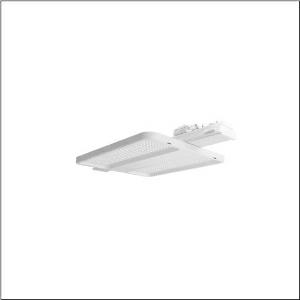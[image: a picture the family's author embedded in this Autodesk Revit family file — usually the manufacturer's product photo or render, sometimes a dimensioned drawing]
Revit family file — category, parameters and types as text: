
# Revit family: highbay_11_fur_licross_r__tragschiene_midi_51hn11da4fla_28e0
name_source: partatom
category: Lighting Fixtures
units: mm (PartAtom-declared; Revit-internal decimal feet)

## family parameters
Cut with Voids When Loaded = No
Host = Face
Light Source = No
Part Type = Normal
Room Calculation Point = No
Round Connector Dimension = Use Diameter
Shared = No

## types (1)
- --- (1 x LED, 15000 lm, 73.2 W, 4000K)
    Apparent Load = 73 VA
    CIE Flux Codes = 85 97 100 100 100
    Color Rendering = 80
    Color Temperature = 4000K
    Default Elevation = 1800 mm
    Description = Highbay 11 for Licross® trunking rail midi, high bay luminaire, primary light control with lens, of PMMA, primary optical cover: cover, of PMMA, light emission: direct distribution, primary light characteristic: symmetric, LED, rated luminous flux: 15.000lm, luminous efficacy: 205lm/W, light colour: 840, colour temperature: 4000K, control gear: DALI 2, with plug, 5-pole, with phase selection, mains connection: 230..240V, AC, 50/60Hz, rated input power: 73.2W, housing frame, of high-performance plastic PA6, matt traffic white (RAL 9016), length: 750mm, width: 442mm, height: 71mm, lever catch, fixing on rail side, of steel, galvanised, white, blank cover, of PC/ABS, traffic white (RAL 9016), protection rating (complete): IP64, insulation class (complete): insulation class I (protective earthing), certification: CE, ENEC, VDE, UKCA, protection symbol: D, impact resistance: IK07, permissible operating ambient temperature: -40..+55°C, corresponds to IFS (International Featured Standards) requirements for safety and quality in the food industry, LABS conformity tested according to VDMA 24364:2018-05, packaging unit: 1 piece
    Height = 72 mm  [stored 0.23622 ft]
    Lamp = 1 x LED
    Lamp Light Flux = 15000 lm
    Lamp Power = 73.2 W
    Lamp count = 1
    Length = 474 mm
    Luminous efficacy = 205 lm/W
    Manufacturer = Siteco
    ModVariant = No
    Model = 51HN11DA4FLA
    Mounting Place = Ceiling
    Mounting Type = Pendant
    Number of Poles = 1
    OnlyDefault = Yes
    Power Factor = 1
    Product Name = Highbay 11 für Licross® Tragschiene midi
    Product group = high bay luminaire
    ProductGroupID = 901
    Protection Class = Protection class I
    Protection Degree = IP 64
    RLX_Detail_Level = 1
    RLX_Emergency_Light_Flux = 0 lm
    RLX_Emergency_Type = 0
    RLX_Emergency_Type_DB = No
    RlxData = <blob elided: 16909 chars, md5=98c1014c>
    Socket = socket
    Standby Power = 0 W
    System Light Flux = 15000 lm
    System Power = 73 W
    Type Comments = factory setting: luminous flux: 100 % | dim-lin: 254 | 339 mA
    Type Image = l_1363258.jpg
    URL = http://relux.com
    VarID = @adj_004991
    Voltage = 0 V
    Weight = 0.00 kg
    Width = 442 mm

note: [stored X ft] marks values corroborated as IEEE doubles in the binary element streams (Revit-internal decimal feet)

## geometry (parser evidence)
native form markers: Blend x4, Sweep x9
no freeform markers — native parametric forms only
